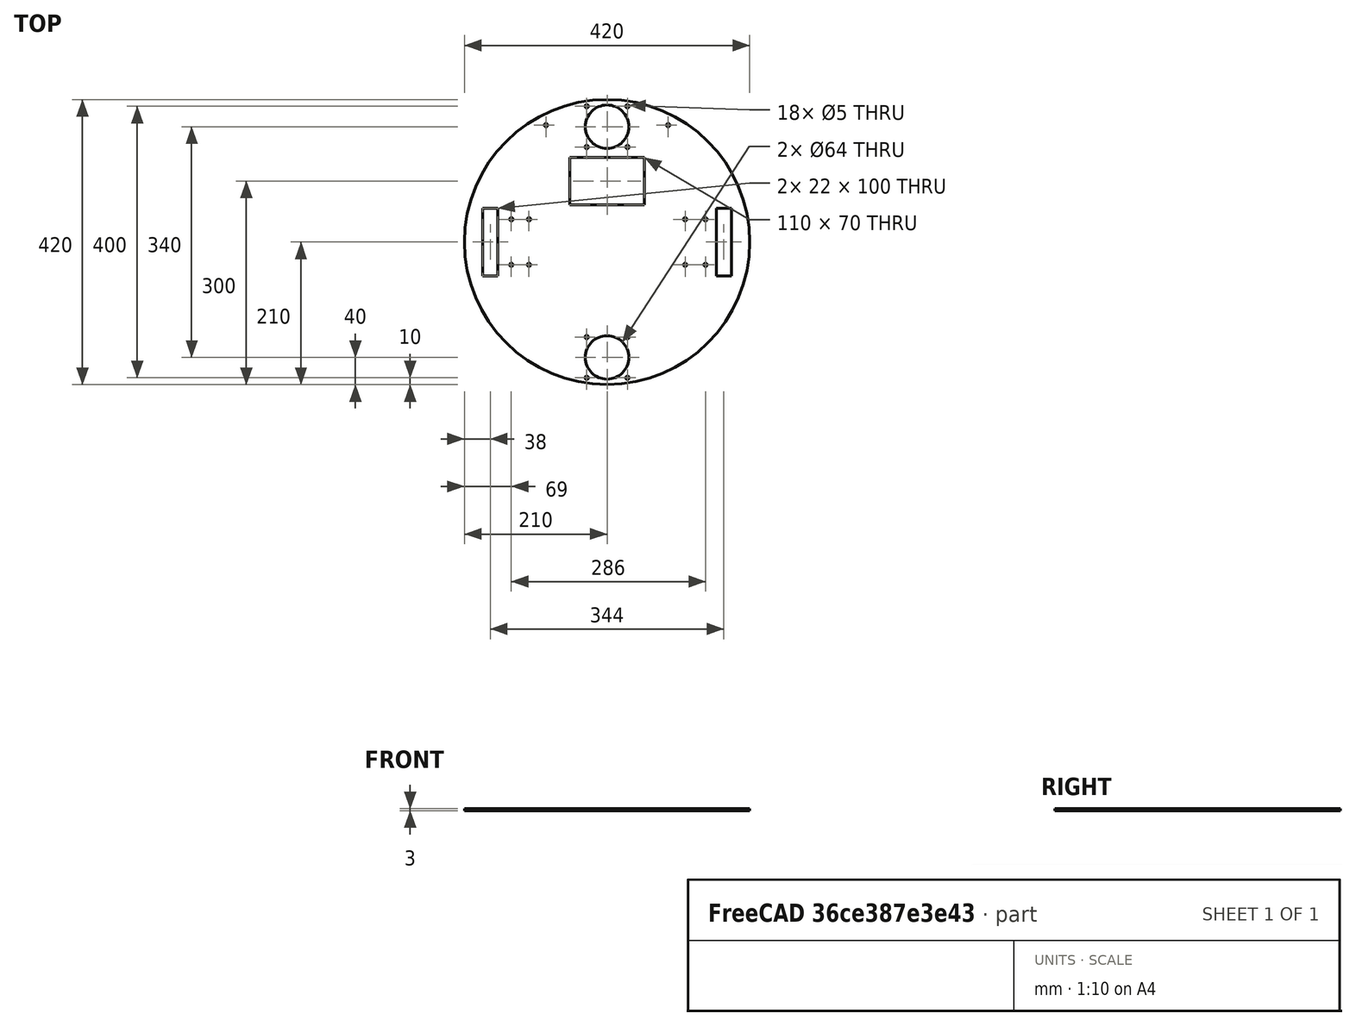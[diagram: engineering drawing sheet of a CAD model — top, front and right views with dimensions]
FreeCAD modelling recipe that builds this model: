
FCSTD DOCUMENT  (FreeCAD 0.15R4671 (Git))
Label: base_0
License: All rights reserved
LicenseURL: http://en.wikipedia.org/wiki/All_rights_reserved
objects: Drawing::FeatureViewPart×3, Sketcher::SketchObject×1, PartDesign::Pad×1, Drawing::FeaturePage×1
note: 3 computed .brp shape members not serialized (recipe doc carries the construction recipe); baked Part::Feature solids carry a one-line shape summary decoded from their .brp

FEATURE [Sketcher::SketchObject] Sketch
  sketch-geometry (33):
    g0: Circle CenterX=0 CenterY=0 CenterZ=0 NormalX=0 NormalY=0 NormalZ=1 Radius=210
    g1: Circle CenterX=0 CenterY=170 CenterZ=0 NormalX=0 NormalY=0 NormalZ=1 Radius=32
    g2: Circle CenterX=0 CenterY=-170 CenterZ=0 NormalX=0 NormalY=0 NormalZ=1 Radius=32
    g3: Circle CenterX=-141 CenterY=33.5 CenterZ=0 NormalX=0 NormalY=0 NormalZ=1 Radius=2.5
    g4: Circle CenterX=-141 CenterY=-33.5 CenterZ=0 NormalX=0 NormalY=0 NormalZ=1 Radius=2.5
    g5: Circle CenterX=-115 CenterY=33.5 CenterZ=0 NormalX=0 NormalY=0 NormalZ=1 Radius=2.5
    g6: Circle CenterX=-115 CenterY=-33.5 CenterZ=0 NormalX=0 NormalY=0 NormalZ=1 Radius=2.5
    g7: LineSegment StartX=-161 StartY=-50 StartZ=0 EndX=-183 EndY=-50 EndZ=0
    g8: LineSegment StartX=-183 StartY=-50 StartZ=0 EndX=-183 EndY=50 EndZ=0
    g9: LineSegment StartX=-183 StartY=50 StartZ=0 EndX=-161 EndY=50 EndZ=0
    g10: LineSegment StartX=-161 StartY=50 StartZ=0 EndX=-161 EndY=-50 EndZ=0
    g11: Circle CenterX=115 CenterY=33.5 CenterZ=0 NormalX=0 NormalY=0 NormalZ=1 Radius=2.5
    g12: Circle CenterX=115 CenterY=-33.5 CenterZ=0 NormalX=0 NormalY=0 NormalZ=1 Radius=2.5
    g13: Circle CenterX=145 CenterY=33.5 CenterZ=0 NormalX=0 NormalY=0 NormalZ=1 Radius=2.5
    g14: Circle CenterX=145 CenterY=-33.5 CenterZ=0 NormalX=0 NormalY=0 NormalZ=1 Radius=2.5
    g15: LineSegment StartX=183 StartY=50 StartZ=0 EndX=161 EndY=50 EndZ=0
    g16: LineSegment StartX=161 StartY=50 StartZ=0 EndX=161 EndY=-50 EndZ=0
    g17: LineSegment StartX=161 StartY=-50 StartZ=0 EndX=183 EndY=-50 EndZ=0
    g18: LineSegment StartX=183 StartY=-50 StartZ=0 EndX=183 EndY=50 EndZ=0
    g19: Circle CenterX=-90 CenterY=172.291 CenterZ=0 NormalX=0 NormalY=0 NormalZ=1 Radius=2.5
    g20: Circle CenterX=90 CenterY=172.291 CenterZ=0 NormalX=0 NormalY=0 NormalZ=1 Radius=2.5
    g21: Circle CenterX=-30 CenterY=200 CenterZ=0 NormalX=0 NormalY=0 NormalZ=1 Radius=2.5
    g22: Circle CenterX=30 CenterY=200 CenterZ=0 NormalX=0 NormalY=0 NormalZ=1 Radius=2.5
    g23: Circle CenterX=-30 CenterY=140 CenterZ=0 NormalX=0 NormalY=0 NormalZ=1 Radius=2.5
    g24: Circle CenterX=30 CenterY=140 CenterZ=0 NormalX=0 NormalY=0 NormalZ=1 Radius=2.5
    g25: Circle CenterX=-30 CenterY=-140 CenterZ=0 NormalX=0 NormalY=0 NormalZ=1 Radius=2.5
    g26: Circle CenterX=30 CenterY=-140 CenterZ=0 NormalX=0 NormalY=0 NormalZ=1 Radius=2.5
    g27: Circle CenterX=-30 CenterY=-200 CenterZ=0 NormalX=0 NormalY=0 NormalZ=1 Radius=2.5
    g28: Circle CenterX=30 CenterY=-200 CenterZ=0 NormalX=0 NormalY=0 NormalZ=1 Radius=2.5
    g29: LineSegment StartX=-55 StartY=125 StartZ=0 EndX=55 EndY=125 EndZ=0
    g30: LineSegment StartX=55 StartY=125 StartZ=0 EndX=55 EndY=55 EndZ=0
    g31: LineSegment StartX=55 StartY=55 StartZ=0 EndX=-55 EndY=55 EndZ=0
    g32: LineSegment StartX=-55 StartY=55 StartZ=0 EndX=-55 EndY=125 EndZ=0
  constraints (75):
    c: Coincident(g0,g-1)
    c: Radius(g0) = 210
    c: PointOnObject(g1,g-2)
    c: PointOnObject(g2,g-2)
    c: Equal(g2,g1)
    c: Equal(g4,g3)
    c: Symmetric(g3,g4,g-1)
    c: Equal(g5,g3)
    c: Equal(g6,g5)
    c: Coincident(g7,g8)
    c: Coincident(g8,g9)
    c: Coincident(g9,g10)
    c: Coincident(g10,g7)
    c: Horizontal(g7)
    c: Horizontal(g9)
    c: Vertical(g8)
    c: Vertical(g10)
    c: Equal(g5,g11)
    c: Equal(g13,g12)
    c: Equal(g12,g14)
    c: Equal(g14,g11)
    c: Coincident(g15,g16)
    c: Coincident(g16,g17)
    c: Coincident(g17,g18)
    c: Coincident(g18,g15)
    c: Horizontal(g15)
    c: Horizontal(g17)
    c: Vertical(g16)
    c: Vertical(g18)
    c: Symmetric(g11,g5,g-2)
    c: Symmetric(g12,g6,g-2)
    c: Symmetric(g14,g13,g-1)
    c: Equal(g10,g16)
    c: Equal(g15,g9)
    c: Symmetric(g15,g9,g-2)
    c: Symmetric(g20,g19,g-2)
    c: DistanceX(g-1,g19) = -90
    c: Radius(g21) = 2.5
    c: Symmetric(g21,g22,g-2)
    c: DistanceX(g-1,g21) = -30
    c: Equal(g21,g22)
    c: Symmetric(g24,g23,g-2)
    c: Equal(g28,g26)
    c: Equal(g26,g25)
    c: Equal(g25,g27)
    c: Equal(g27,g21)
    c: Symmetric(g27,g28,g-2)
    c: Symmetric(g26,g25,g-2)
    c: Symmetric(g23,g25,g-1)
    c: Symmetric(g21,g27,g-1)
    c: Equal(g19,g21)
    c: Equal(g20,g21)
    c: DistanceY(g8) = 100
    c: DistanceX(g7) = -22
    c: DistanceY(g23,g21) = 60
    c: DistanceX(g23,g24) = 60
    c: Symmetric(g9,g7,g-1)
    c: DistanceX(g3,g9) = -20
    c: DistanceY(g-1,g1) = 170
    c: Symmetric(g2,g1,g-1)
    c: DistanceY(g22,g1) = -30
    c: Coincident(g29,g30)
    c: Coincident(g30,g31)
    c: Coincident(g31,g32)
    c: Coincident(g32,g29)
    c: Horizontal(g29)
    c: Horizontal(g31)
    c: Vertical(g30)
    c: Vertical(g32)
    c: DistanceY(g32) = 70
    c: DistanceX(g31) = -110
    c: Symmetric(g31,g30,g-2)
    c: Radius(g2) = 32
    c: DistanceX(g-1,g7) = -161
    c: DistanceY(g-1,g29) = 125
FEATURE [PartDesign::Pad] Pad
  Length = 3
  Length2 = 100
  Midplane = true
  Sketch = -> Sketch
  Type = 0
FEATURE [Drawing::FeatureViewPart] Ortho  label="Ortho_0_0"
  Direction = (1,0,0)
  HiddenWidth = 0.15
  LineWidth = 0.35
  Rotation = -90
  Scale = 0.25
  ShowHiddenLines = false
  ShowSmoothLines = false
  Source = -> Pad
  Tolerance = 0.05
  ViewResult = <g id="Ortho_0_0"\n   transform="rotate(-90,91.5,147.542) translate(91.5,147.542) scale(0.25,0.25)"\n  >\n<g   stroke="rgb(0, 0, 0)"\n   stroke-width="1.4"\n   stroke-linecap="butt"\n   stroke-linejoin="miter"\n   fill="none"\n   transform="scale(1,-1)"\n  >\n<path id= "1" d=" M 1.5 210 L -1.5 210 " />\n<path id= "2" d=" M 1.5 -210 L -1.5 -210 " />\n</g>\n<g   stroke="rgb(0, 0, 0)"\n   stroke-width="1.4"\n   stroke-linecap="butt"\n   stroke-linejoin="miter"\n   fill="none"\n   transform="scale(1,-1)"\n  >\n<path d="M-1.5,0 L-1.5,-23.5125  L-1.5,-46.7294  L-1.5,-69.3586  L-1.5,-91.1156  L-1.5,-111.727  L-1.5,-130.933  L-1.5,-148.492  L-1.5,-164.185  L-1.5,-177.812  L-1.5,-189.203  L-1.5,-198.215  L-1.5,-204.735  L-1.5,-208.68  L-1.5,-210 " /><path d="M-1.5,210 L-1.5,208.68  L-1.5,204.735  L-1.5,198.215  L-1.5,189.203  L-1.5,177.812  L-1.5,164.185  L-1.5,148.492  L-1.5,130.933  L-1.5,111.727  L-1.5,91.1156  L-1.5,69.3586  L-1.5,46.7294  L-1.5,23.5125  L-1.5,5.14352e-14 " /><path d="M1.5,0 L1.5,-23.5125  L1.5,-46.7294  L1.5,-69.3586  L1.5,-91.1156  L1.5,-111.727  L1.5,-130.933  L1.5,-148.492  L1.5,-164.185  L1.5,-177.812  L1.5,-189.203  L1.5,-198.215  L1.5,-204.735  L1.5,-208.68  L1.5,-210 " /><path d="M1.5,210 L1.5,208.68  L1.5,204.735  L1.5,198.215  L1.5,189.203  L1.5,177.812  L1.5,164.185  L1.5,148.492  L1.5,130.933  L1.5,111.727  L1.5,91.1156  L1.5,69.3586  L1.5,46.7294  L1.5,23.5125  L1.5,5.14352e-14 " /></g>\n</g>
  Visible = true
  X = 91.5
  Y = 147.542
FEATURE [Drawing::FeatureViewPart] Ortho002  label="Ortho_1_1"
  Direction = (0.57735,0.57735,0.57735)
  HiddenWidth = 0.15
  LineWidth = 0.35
  Rotation = 120
  Scale = 0.25
  ShowHiddenLines = false
  ShowSmoothLines = false
  Source = -> Pad
  Tolerance = 0.05
  ViewResult = <blob: 7616 chars omitted>
  Visible = true
  X = 215.5
  Y = 78.5833
FEATURE [Drawing::FeatureViewPart] Ortho003  label="Ortho_0_1"
  Direction = (0,0,1)
  HiddenWidth = 0.15
  LineWidth = 0.35
  Rotation = 90
  Scale = 0.25
  ShowHiddenLines = false
  ShowSmoothLines = false
  Source = -> Pad
  Tolerance = 0.05
  ViewResult = <g id="Ortho_0_1"\n   transform="rotate(90,91.5,78.5833) translate(91.5,78.5833) scale(0.25,0.25)"\n  >\n<g   stroke="rgb(0, 0, 0)"\n   stroke-width="1.4"\n   stroke-linecap="butt"\n   stroke-linejoin="miter"\n   fill="none"\n   transform="scale(1,-1)"\n  >\n<circle cx ="0" cy ="0" r ="210" /><path id= "2" d=" M -55 125 L 55 125 " />\n<path id= "3" d=" M 55 125 L 55 55 " />\n<path id= "4" d=" M 55 55 L -55 55 " />\n<path id= "5" d=" M -55 55 L -55 125 " />\n<path id= "6" d=" M -161 -50 L -183 -50 " />\n<path id= "7" d=" M -183 -50 L -183 50 " />\n<path id= "8" d=" M -183 50 L -161 50 " />\n<path id= "9" d=" M -161 50 L -161 -50 " />\n<path id= "10" d=" M 183 50 L 161 50 " />\n<path id= "11" d=" M 161 50 L 161 -50 " />\n<path id= "12" d=" M 161 -50 L 183 -50 " />\n<path id= "13" d=" M 183 -50 L 183 50 " />\n<circle cx ="0" cy ="170" r ="32" /><circle cx ="0" cy ="-170" r ="32" /><circle cx ="90" cy ="172.291" r ="2.5" /><circle cx ="-90" cy ="172.291" r ="2.5" /><circle cx ="-141" cy ="33.5" r ="2.5" /><circle cx ="-141" cy ="-33.5" r ="2.5" /><circle cx ="-115" cy ="33.5" r ="2.5" /><circle cx ="-115" cy ="-33.5" r ="2.5" /><circle cx ="30" cy ="-200" r ="2.5" /><circle cx ="115" cy ="33.5" r ="2.5" /><circle cx ="115" cy ="-33.5" r ="2.5" /><circle cx ="145" cy ="-33.5" r ="2.5" /><circle cx ="-30" cy ="-200" r ="2.5" /><circle cx ="-30" cy ="200" r ="2.5" /><circle cx ="30" cy ="200" r ="2.5" /><circle cx ="-30" cy ="140" r ="2.5" /><circle cx ="30" cy ="140" r ="2.5" /><circle cx ="-30" cy ="-140" r ="2.5" /><circle cx ="30" cy ="-140" r ="2.5" /><circle cx ="145" cy ="33.5" r ="2.5" /></g>\n</g>
  Visible = true
  X = 91.5
  Y = 78.5833
FEATURE [Drawing::FeaturePage] Page
  EditableTexts = Siqueira | Tuane | Pindí | Drawing | Base 0 | 0020 | 2015-06-21
  Group = -> [Ortho,Ortho002,Ortho003]
  Template = <path>
note: 1 file-system path scrubbed to <path> (originals preserved in the JSON sidecar)
